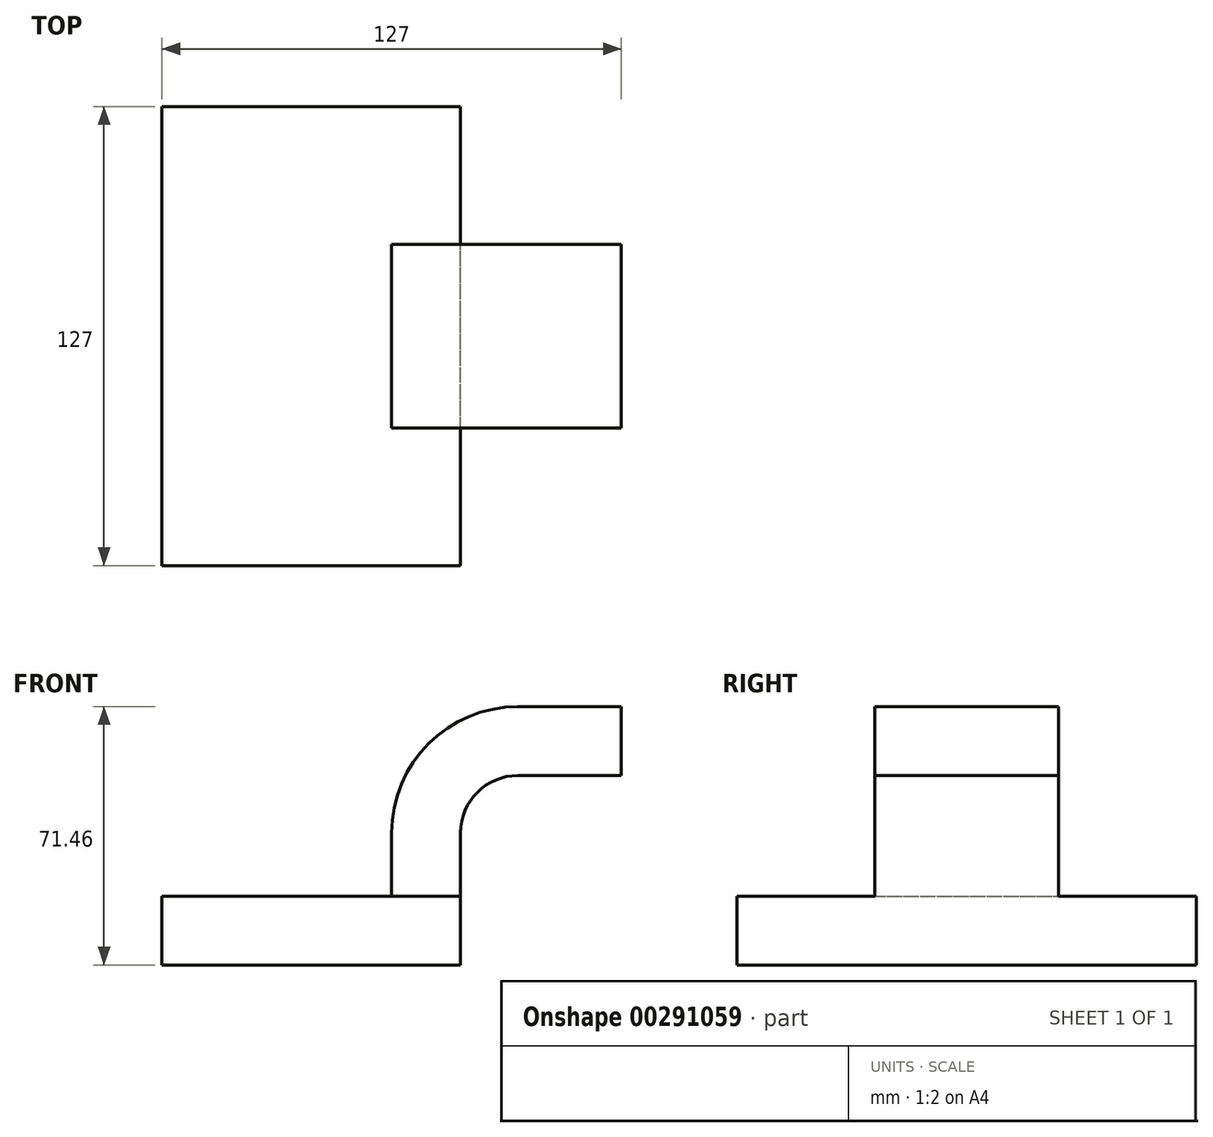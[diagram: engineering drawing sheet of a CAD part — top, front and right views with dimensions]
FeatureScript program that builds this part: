
annotation { "Feature Type Name" : "Feature", "Feature Type Description" : "" }
export const myFeature = defineFeature(function(context is Context, id is Id, definition is map)
    precondition{}
    {
        {
            var Q0;
            Q0=qCreatedBy(makeId("Front.planeOp"),FACE);
            var sketch = newSketch(context, id + "F0", { "sketchPlane" : qUnion([Q0])});
            skLineSegment(sketch, "E0.bottom", {"start": v(41.28, 9.53) * mm, "end": v(-41.28, 9.53) * mm});
            skLineSegment(sketch, "E0.top", {"start": v(41.28, -9.53) * mm, "end": v(-41.28, -9.53) * mm});
            skLineSegment(sketch, "E0.left", {"start": v(41.28, 9.52) * mm, "end": v(41.28, -9.53) * mm});
            skLineSegment(sketch, "E0.right", {"start": v(-41.28, 9.53) * mm, "end": v(-41.28, -9.53) * mm});
            skPoint(sketch, "E0.middle", {"position": v(0, 0) * mm});
            skLineSegment(sketch, "E1.bottom", {"start": v(111.13, 66.67) * mm, "end": v(60.33, 66.67) * mm});
            skLineSegment(sketch, "E1.top", {"start": v(111.13, 38.1) * mm, "end": v(60.33, 38.1) * mm});
            skLineSegment(sketch, "E1.left", {"start": v(111.13, 66.67) * mm, "end": v(111.13, 38.1) * mm});
            skLineSegment(sketch, "E1.right", {"start": v(60.33, 66.67) * mm, "end": v(60.33, 38.1) * mm});
            skPoint(sketch, "E1.middle", {"position": v(85.73, 52.39) * mm});
            skLineSegment(sketch, "E2", {"start": v(41.28, 9.53) * mm, "end": v(41.28, 27) * mm});
            skArc(sketch, "E3", {"start": v(41.28, 27) * mm, "mid": v(45.92, 38.23) * mm, "end": v(57.15, 42.88) * mm});
            skLineSegment(sketch, "E4", {"start": v(57.15, 42.88) * mm, "end": v(85.73, 42.88) * mm});
            skLineSegment(sketch, "E5.0", {"start": v(57.15, 61.93) * mm, "end": v(85.73, 61.93) * mm});
            skArc(sketch, "E5.1", {"start": v(22.23, 27) * mm, "mid": v(32.45, 51.7) * mm, "end": v(57.15, 61.93) * mm});
            skLineSegment(sketch, "E5.2", {"start": v(22.23, 9.53) * mm, "end": v(22.23, 27) * mm});
            skLineSegment(sketch, "E6", {"start": v(85.73, 38.1) * mm, "end": v(85.73, 66.67) * mm});
            skFitSpline(sketch, "E7", {"points": [v(-41.28, 9.52) * mm, v(57.15, 61.93) * mm], "startDerivative": vector(3.85, 112.9) * mm, "endDerivative": vector(127.65, -2.35) * mm});
            skSolve(sketch);
        }
        {
            var Q0;
            Q0=makeQuery(id+"F0.imprint","IMPRINT",FACE,{"disambiguationData":[TD([[makeQuery(id+"F0.imprint","IMPRINT",EDGE,{"derivedFrom":sQuery(id+"F0.wireOp",EDGE,"E0.top")}),-1.0]])]});
            extrude(context, id + "F1", {"entities" : qUnion([Q0]), "endBound" : BoundingType.SYMMETRIC, "depth" : 127 * mm});
        }
        {
            var Q0;
            {var subQ1=sQuery(id+"F0.wireOp",EDGE,"E2");Q0=makeQuery(id+"F0.imprint","IMPRINT",FACE,{"disambiguationData":[TD([[makeQuery(id+"F0.imprint","IMPRINT",EDGE,{"derivedFrom":subQ1}),1.0]])]});}
            var Q1;
            {var subQ0=sQuery(id+"F0.wireOp",EDGE,"E5.0");var subQ1=sQuery(id+"F0.wireOp",EDGE,"E1.right");var subQ2=makeQuery(id+"F0.imprint","INTERSECT",VERTEX,{"derivedFrom":[subQ1,subQ0]});Q1=makeQuery(id+"F0.imprint","IMPRINT",FACE,{"disambiguationData":[TD([[makeQuery(id+"F0.imprint","IMPRINT",EDGE,{"disambiguationData":[TD([[subQ2,-1.0]])],"derivedFrom":subQ1}),1.0]])]});}
            extrude(context, id + "F2", {"entities" : qUnion([Q0, Q1]), "operationType" : NewBodyOperationType.ADD, "endBound" : BoundingType.SYMMETRIC, "depth" : 50.8 * mm});
        }
        {
            var Q0;
            Q0=makeQuery(id+"F0.imprint","IMPRINT",FACE,{"disambiguationData":[TD([[makeQuery(id+"F0.imprint","IMPRINT",EDGE,{"derivedFrom":sQuery(id+"F0.wireOp",EDGE,"E5.1")}),1.0]])]});
            extrude(context, id + "F3", {"entities" : qUnion([Q0]), "operationType" : NewBodyOperationType.ADD, "depth" : 15.88 * mm});
        }
    });
